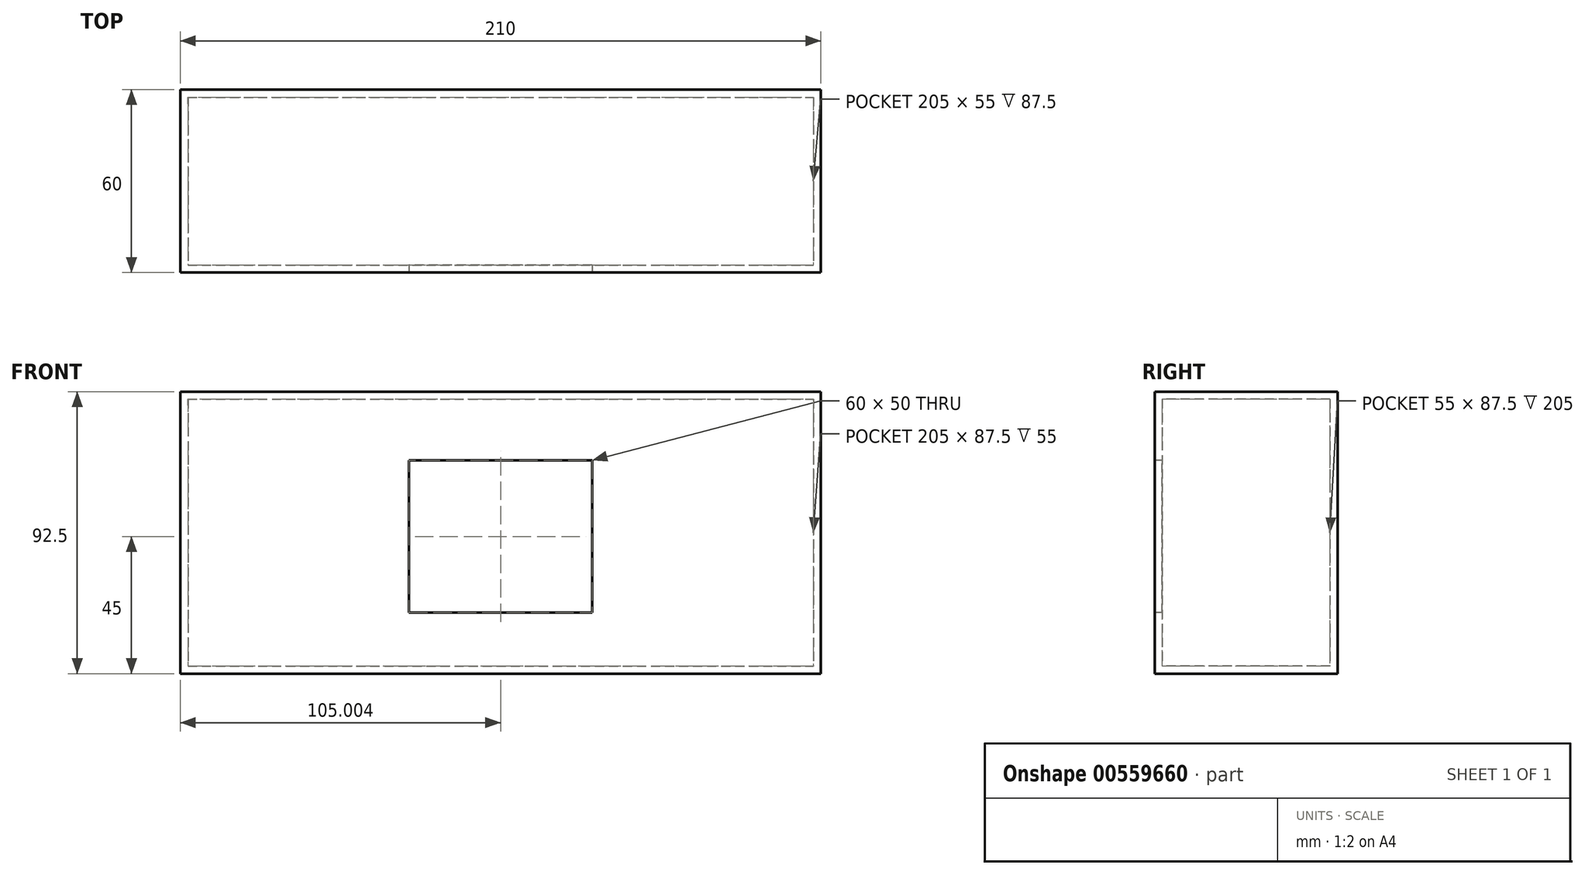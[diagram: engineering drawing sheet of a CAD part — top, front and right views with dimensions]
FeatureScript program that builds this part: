
annotation { "Feature Type Name" : "Feature", "Feature Type Description" : "" }
export const myFeature = defineFeature(function(context is Context, id is Id, definition is map)
    precondition{}
    {
        {
            var Q0;
            Q0=qCreatedBy(makeId("Top.planeOp"),FACE);
            var sketch = newSketch(context, id + "F0", { "sketchPlane" : qUnion([Q0])});
            skLineSegment(sketch, "E0.bottom", {"start": v(-102.56, -11.24) * mm, "end": v(107.44, -11.24) * mm});
            skLineSegment(sketch, "E0.top", {"start": v(-102.56, -71.24) * mm, "end": v(107.44, -71.24) * mm});
            skLineSegment(sketch, "E0.left", {"start": v(-102.56, -11.24) * mm, "end": v(-102.56, -71.24) * mm});
            skLineSegment(sketch, "E0.right", {"start": v(107.44, -11.24) * mm, "end": v(107.44, -71.24) * mm});
            skSolve(sketch);
        }
        {
            var Q0;
            Q0=makeQuery(id+"F0.imprint","IMPRINT",FACE,{"disambiguationData":[TD([[makeQuery(id+"F0.imprint","IMPRINT",EDGE,{"derivedFrom":sQuery(id+"F0.wireOp",EDGE,"E0.bottom")}),-1.0]])]});
            extrude(context, id + "F1", {"entities" : qUnion([Q0]), "depth" : 90 * mm, "offsetDistance" : 25 * mm});
        }
        {
            var Q0;
            Q0=makeQuery(id+"F1.opExtrude","CAP_FACE",FACE,{"disambiguationData":[OSD([sQuery(id+"F0.wireOp",EDGE,"E0.bottom"),sQuery(id+"F0.wireOp",EDGE,"E0.top"),sQuery(id+"F0.wireOp",EDGE,"E0.left"),sQuery(id+"F0.wireOp",EDGE,"E0.right")])],"isStart":false});
            shell(context, id + "F2", {"entities" : qUnion([Q0]), "thickness" : 2.5 * mm});
        }
        {
            var Q0;
            Q0=makeQuery(id+"F1.opExtrude","CAP_FACE",FACE,{"disambiguationData":[OSD([sQuery(id+"F0.wireOp",EDGE,"E0.bottom"),sQuery(id+"F0.wireOp",EDGE,"E0.top"),sQuery(id+"F0.wireOp",EDGE,"E0.left"),sQuery(id+"F0.wireOp",EDGE,"E0.right")])],"isStart":false});
            var sketch = newSketch(context, id + "F3", { "sketchPlane" : qUnion([Q0])});
            skLineSegment(sketch, "E1.bottom", {"start": v(-102.56, -11.24) * mm, "end": v(107.44, -11.24) * mm});
            skLineSegment(sketch, "E1.top", {"start": v(-102.56, -71.24) * mm, "end": v(107.44, -71.24) * mm});
            skLineSegment(sketch, "E1.left", {"start": v(-102.56, -11.24) * mm, "end": v(-102.56, -71.24) * mm});
            skLineSegment(sketch, "E1.right", {"start": v(107.44, -11.24) * mm, "end": v(107.44, -71.24) * mm});
            skSolve(sketch);
        }
        {
            var Q0;
            Q0=makeQuery(id+"F3.imprint","IMPRINT",FACE,{"disambiguationData":[TD([[makeQuery(id+"F3.imprint","IMPRINT",EDGE,{"derivedFrom":sQuery(id+"F3.wireOp",EDGE,"E1.bottom")}),-1.0]])]});
            var Q1;
            {var subQ0=sQuery(id+"F0.wireOp",EDGE,"E0.bottom");Q1=makeQuery(id+"F3.imprint","IMPRINT",FACE,{"disambiguationData":[TD([[makeQuery(id+"F3.imprint","IMPRINT",EDGE,{"derivedFrom":makeQuery(id+"F2.opShell","OFFSET_EDGE",EDGE,{"disambiguationData":[OSD([subQ0]),TDD([makeQuery(id+"F1.opExtrude","CAP_EDGE",EDGE,{"disambiguationData":[OSD([subQ0])],"isStart":false})])]})}),-1.0]])]});}
            extrude(context, id + "F4", {"entities" : qUnion([Q0, Q1]), "operationType" : NewBodyOperationType.ADD, "depth" : 2.5 * mm, "offsetDistance" : 25 * mm});
        }
        {
            var Q0;
            Q0=makeQuery(id+"F4.boolean.opBoolean","MERGE",FACE,{"derivedFrom":[makeQuery(id+"F1.opExtrude","SWEPT_FACE",FACE,{"disambiguationData":[OSD([sQuery(id+"F0.wireOp",EDGE,"E0.top")])]}),makeQuery(id+"F4.opExtrude","SWEPT_FACE",FACE,{"disambiguationData":[OSD([sQuery(id+"F3.wireOp",EDGE,"E1.top")])]})]});
            var sketch = newSketch(context, id + "F5", { "sketchPlane" : qUnion([Q0])});
            skLineSegment(sketch, "E2.bottom", {"start": v(-27.56, 70) * mm, "end": v(32.44, 70) * mm});
            skLineSegment(sketch, "E2.top", {"start": v(-27.56, 20) * mm, "end": v(32.44, 20) * mm});
            skLineSegment(sketch, "E2.left", {"start": v(-27.56, 70) * mm, "end": v(-27.56, 20) * mm});
            skLineSegment(sketch, "E2.right", {"start": v(32.44, 70) * mm, "end": v(32.44, 20) * mm});
            skSolve(sketch);
        }
        {
            var Q0;
            Q0=makeQuery(id+"F5.imprint","IMPRINT",FACE,{"disambiguationData":[TD([[makeQuery(id+"F5.imprint","IMPRINT",EDGE,{"derivedFrom":sQuery(id+"F5.wireOp",EDGE,"E2.bottom")}),-1.0]])]});
            extrude(context, id + "F6", {"entities" : qUnion([Q0]), "operationType" : NewBodyOperationType.REMOVE, "oppositeDirection" : true, "depth" : 25 * mm, "offsetDistance" : 25 * mm});
        }
    });
